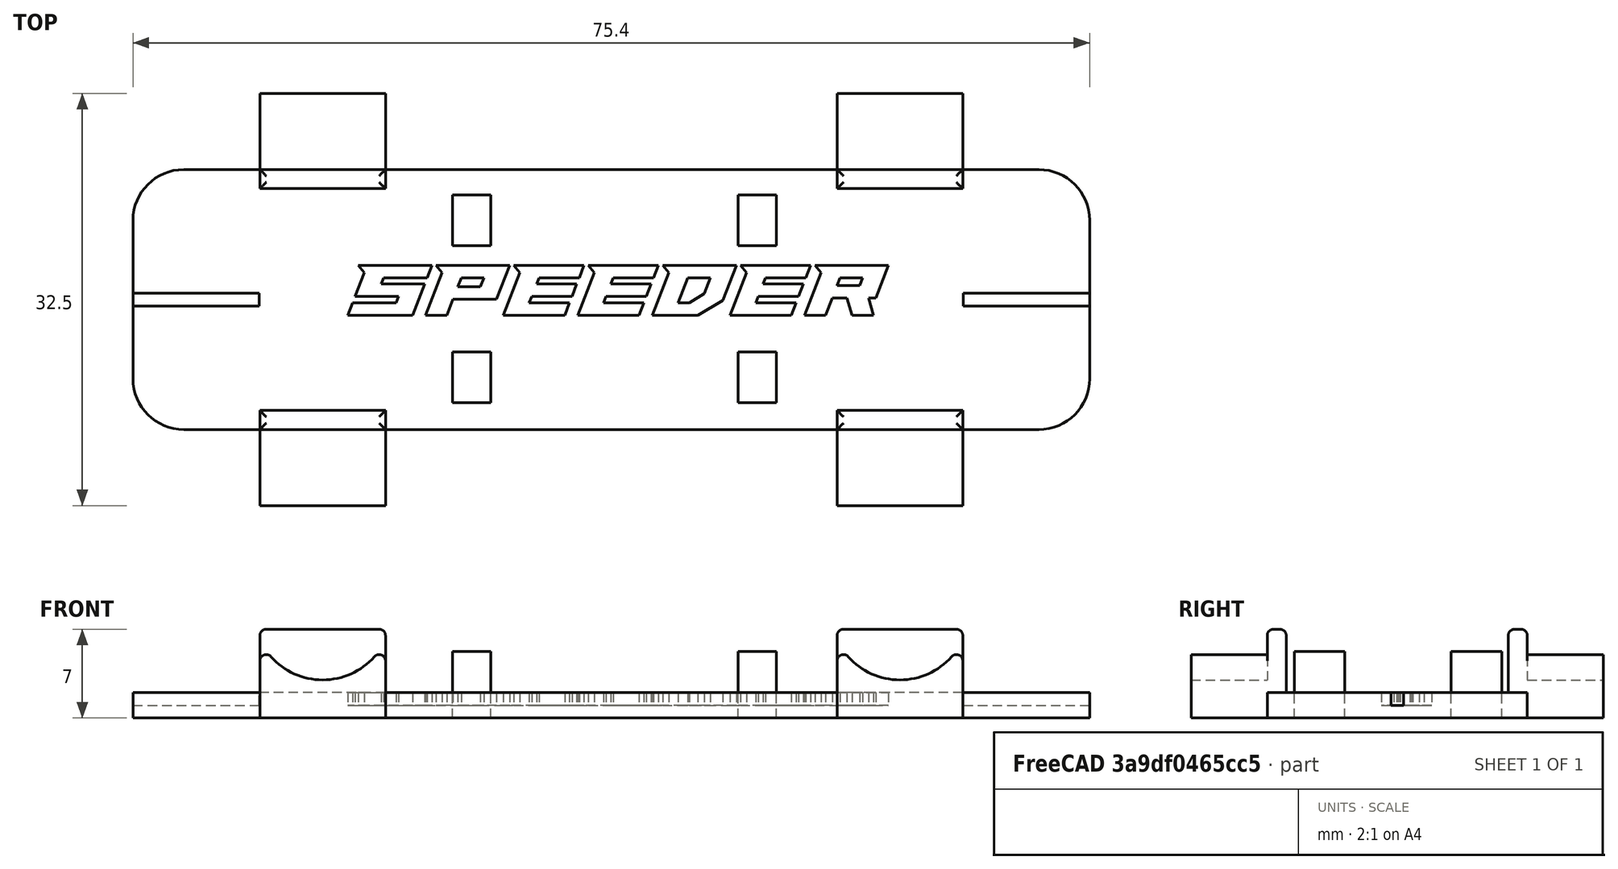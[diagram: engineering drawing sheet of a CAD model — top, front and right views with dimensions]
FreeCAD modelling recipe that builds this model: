
FCSTD DOCUMENT  (FreeCAD 0.19R24276 (Git))
Label: axleJig5
License: All rights reserved
LicenseURL: http://en.wikipedia.org/wiki/All_rights_reserved
objects: Part::Box×15, Part::Fillet×7, Part::Cut×6, Part::MultiFuse×4, Part::Cylinder×2, Spreadsheet::Sheet×1, Part::Part2DObjectPython×1, Part::Extrusion×1
note: 36 computed .brp shape members not serialized (recipe doc carries the construction recipe); baked Part::Feature solids carry a one-line shape summary decoded from their .brp

FEATURE [Part::Box] Box  label="Cube"
  AttacherType = Attacher::AttachEngine3D
  Height = 8
  Length = 9.9
  Placement = pos=(-4.95,0,0) rot=(0,0,1;0rad)
  Width = 32.5
  expr: Width = <<data>>.wheel_width * 2 + <<data>>.axle_width
  expr: Length = Spreadsheet.wheel_diameter_F - 1mm
  expr: .Placement.Base.x = -<<data>>.wheel_diameter_F / 2 + 0.5mm
FEATURE [Spreadsheet::Sheet] Spreadsheet  label="data"
  cells = A4=wheel_base; B4(wheel_base)==45.5mm; C4=add 0.5mm; D4==43.4mm; E4==46.2mm; F4==44.25mm; A5=axle_width; B5(axle_width)==20.5mm; C5=inside wheel-to-wheel; D5=21; E5=21.mm; F5==21mm; A6=wheel_well; B6(wheel_well)==17.5mm; D6==16.75mm; E6==17mm; F6=16.5; A7=ride_height_r; B7(ride_height_r)==2.25mm; D7==3.75mm; F7==2mm; A8=ride_height_f; B8(ride_height_f)==2.25mm; A9=axle_diameter; A10=post_wdith; A11=post_thickness; A12=wheel_diameter_F; B12(wheel_diameter_F)==10.9mm; D12==10.9mm; E12==10.9mm; F12==10.9mm; A13=wheel_diameter_R; B13(wheel_diameter_R)==10.9mm; D13==10.9mm; E13==10.9mm; F13==12.6mm; A14=wheel_width; B14(wheel_width)==6mm; D14==6mm; E14==6mm; F14=6; B15=Project; D15=Honda Civic Si; E15=Kia Stinger; F15=Rodger Dodger
FEATURE [Part::Cylinder] Cylinder
  Angle = 360
  AttacherType = Attacher::AttachEngine3D
  Height = 32.5
  Placement = pos=(0,0,8.45) rot=(-1,0,0;1.5708rad)
  Radius = 5.45
  expr: Radius = <<data>>.wheel_diameter_F / 2
  expr: Height = <<data>>.wheel_width * 2 + <<data>>.axle_width
  expr: .Placement.Base.z = <<data>>.wheel_diameter_F / 2 + 3mm
FEATURE [Part::Box] Box019  label="Cube017"
  AttacherType = Attacher::AttachEngine3D
  Height = 10
  Length = 9.9
  Placement = pos=(-4.95,6.5,2) rot=(0,0,1;0rad)
  Width = 18.5
  expr: .Placement.Base.y = <<data>>.wheel_width + (<<data>>.axle_width - <<data>>.wheel_well) / 2 - 1mm
  expr: Width = <<data>>.wheel_well + 1mm
  expr: Length = Spreadsheet.wheel_diameter_F - 1mm
  expr: .Placement.Base.x = -<<data>>.wheel_diameter_F / 2 + 0.5mm
FEATURE [Part::Cut] Cut
  Base = -> Box
  Tool = -> Cylinder
FEATURE [Part::Fillet] Fillet
  Base = -> Cut
  Edges = 2 edges r=0.5: [Edge2,Edge9]
FEATURE [Part::Box] Box020  label="FR spacer"
  AttacherType = Attacher::AttachEngine3D
  Height = 7
  Length = 9.9
  Placement = pos=(-4.95,6,0) rot=(0,0,1;0rad)
  Width = 1.5
  expr: Length = Spreadsheet.wheel_diameter_F - 1mm
  expr: .Placement.Base.x = -<<data>>.wheel_diameter_F / 2 + 0.5mm
  expr: .Placement.Base.y = <<data>>.wheel_width
  expr: Width = (<<data>>.axle_width - <<data>>.wheel_well) / 2
FEATURE [Part::Fillet] Fillet001
  Base = -> Box020
  Edges = 4 edges r=0.5: [Edge2,Edge6,Edge10,Edge12]
FEATURE [Part::Cut] Cut007
  Base = -> Fillet
  Tool = -> Box019
FEATURE [Part::Box] Box021  label="RL spacer"
  AttacherType = Attacher::AttachEngine3D
  Height = 7
  Length = 9.9
  Placement = pos=(-4.95,6,0) rot=(0,0,1;0rad)
  Width = 1.5
  expr: Width = (<<data>>.axle_width - <<data>>.wheel_well) / 2
  expr: .Placement.Base.y = <<data>>.wheel_width
  expr: .Placement.Base.x = -<<data>>.wheel_diameter_F / 2 + 0.5mm
  expr: Length = Spreadsheet.wheel_diameter_F - 1mm
FEATURE [Part::Fillet] Fillet002
  Base = -> Box021
  Edges = 4 edges r=0.5: [Edge2,Edge6,Edge10,Edge12]
  Placement = pos=(0,19,0) rot=(0,0,1;0rad)
  expr: .Placement.Base.y = <<data>>.axle_width - (<<data>>.axle_width - <<data>>.wheel_well) / 2
FEATURE [Part::MultiFuse] Fusion  label="FrontAxle"
  Placement = pos=(45.5,0,0) rot=(0,0,1;0rad)
  Shapes = -> [Fillet002,Cut007,Fillet001]
  expr: .Placement.Base.x = <<data>>.wheel_base
FEATURE [Part::Part2DObjectPython] ShapeString  # Draft 2D object (typed FeaturePython)
  FontFile = <userpath>/git/KiCad/Inkscape/fonts/Paladins-nl8P.otf
  Placement = pos=(1.26,15,2) rot=(0,0,1;0rad)
  Size = 2
  String = Speeder
  Tracking = 0
FEATURE [Part::Box] Box022  label="Cube020"
  AttacherType = Attacher::AttachEngine3D
  Height = 10
  Length = 9.9
  Placement = pos=(-4.95,6.5,2) rot=(0,0,1;0rad)
  Width = 18.5
  expr: .Placement.Base.x = -<<data>>.wheel_diameter_R / 2 + 0.5mm
  expr: Length = Spreadsheet.wheel_diameter_R - 1mm
  expr: Width = <<data>>.wheel_well + 1mm
  expr: .Placement.Base.y = <<data>>.wheel_width + (<<data>>.axle_width - <<data>>.wheel_well) / 2 - 1mm
FEATURE [Part::Box] Box023  label="Cube021"
  AttacherType = Attacher::AttachEngine3D
  Height = 7
  Length = 9.9
  Placement = pos=(-4.95,6,0) rot=(0,0,1;0rad)
  Width = 1.5
  expr: Width = (<<data>>.axle_width - <<data>>.wheel_well) / 2
  expr: .Placement.Base.y = <<data>>.wheel_width
  expr: .Placement.Base.x = -Spreadsheet.wheel_diameter_R / 2 + 0.5mm
  expr: Length = Spreadsheet.wheel_diameter_R - 1mm
FEATURE [Part::Fillet] Fillet004
  Base = -> Box023
  Edges = 4 edges r=0.5: [Edge2,Edge6,Edge10,Edge12]
FEATURE [Part::Box] Box024  label="Cube022"
  AttacherType = Attacher::AttachEngine3D
  Height = 7
  Length = 9.9
  Placement = pos=(-4.95,6,0) rot=(0,0,1;0rad)
  Width = 1.5
  expr: Length = Spreadsheet.wheel_diameter_R - 1mm
  expr: .Placement.Base.x = -<<data>>.wheel_diameter_R / 2 + 0.5mm
  expr: .Placement.Base.y = <<data>>.wheel_width
  expr: Width = (<<data>>.axle_width - <<data>>.wheel_well) / 2
FEATURE [Part::Fillet] Fillet005
  Base = -> Box024
  Edges = 4 edges r=0.5: [Edge2,Edge6,Edge10,Edge12]
  Placement = pos=(0,19,0) rot=(0,0,1;0rad)
  expr: .Placement.Base.y = <<data>>.axle_width - (<<data>>.axle_width - <<data>>.wheel_well) / 2
FEATURE [Part::Box] Box025  label="Cube023"
  AttacherType = Attacher::AttachEngine3D
  Height = 8
  Length = 9.9
  Placement = pos=(-4.95,0,0) rot=(0,0,1;0rad)
  Width = 32.5
  expr: .Placement.Base.x = -Spreadsheet.wheel_diameter_R / 2 + 0.5mm
  expr: Length = Spreadsheet.wheel_diameter_R - 1mm
  expr: Width = <<data>>.wheel_width * 2 + <<data>>.axle_width
FEATURE [Part::Cylinder] Cylinder002
  Angle = 360
  AttacherType = Attacher::AttachEngine3D
  Height = 32.5
  Placement = pos=(0,0,8.45) rot=(-1,0,0;1.5708rad)
  Radius = 5.45
  expr: .Placement.Base.z = <<data>>.wheel_diameter_R / 2 + 3mm
  expr: Height = <<data>>.wheel_width * 2 + <<data>>.axle_width
  expr: Radius = <<data>>.wheel_diameter_R / 2
FEATURE [Part::Cut] Cut008
  Base = -> Box025
  Tool = -> Cylinder002
FEATURE [Part::Fillet] Fillet003
  Base = -> Cut008
  Edges = 2 edges r=0.5: [Edge2,Edge9]
FEATURE [Part::Cut] Cut009
  Base = -> Fillet003
  Tool = -> Box022
FEATURE [Part::MultiFuse] Fusion001  label="RearAxle001"
  Shapes = -> [Fillet005,Cut009,Fillet004]
FEATURE [Part::Extrusion] Extrude
  Base = -> ShapeString
  Dir = (0,0,1)
  DirMode = 2
  FaceMakerClass = Part::FaceMakerBullseye
  LengthFwd = 1
  LengthRev = 0
  Reversed = true
  Solid = false
  Symmetric = false
FEATURE [Part::Box] Box026  label="Cube024"
  AttacherType = Attacher::AttachEngine3D
  Height = 1
  Length = 10
  Placement = pos=(-15,15.75,1) rot=(0,0,1;0rad)
  Width = 1
  expr: .Placement.Base.y = (<<data>>.wheel_width * 2 + <<data>>.axle_width) / 2 - 0.5mm
FEATURE [Part::Box] Box027  label="Cube025"
  AttacherType = Attacher::AttachEngine3D
  Height = 1
  Length = 10
  Placement = pos=(50.5,15.75,1) rot=(0,0,1;0rad)
  Width = 1
  expr: .Placement.Base.y = (<<data>>.wheel_width * 2 + <<data>>.axle_width) / 2 - 0.5mm
  expr: .Placement.Base.x = <<data>>.wheel_base + 5mm
FEATURE [Part::Box] Box008  label="base"
  AttacherType = Attacher::AttachEngine3D
  Height = 2
  Length = 75.4
  Placement = pos=(-14.95,6,0) rot=(0,0,1;0rad)
  Width = 20.5
  expr: .Placement.Base.y = <<data>>.wheel_width
  expr: Height = 2mm
  expr: Width = <<data>>.axle_width
  expr: Length = <<data>>.wheel_diameter_F / 2 + <<data>>.wheel_base + <<data>>.wheel_diameter_R / 2 - 1mm + 20mm
  expr: .Placement.Base.x = -<<data>>.wheel_diameter_F / 2 + 0.5mm - 10mm
FEATURE [Part::Fillet] Fillet006
  Base = -> Box008
  Edges = 4 edges r=4: [Edge1,Edge3,Edge5,Edge7]
FEATURE [Part::MultiFuse] Fusion002
  Shapes = -> [Box027,Box026]
FEATURE [Part::Cut] Cut010
  Base = -> Fillet006
  Tool = -> Fusion002
FEATURE [Part::Box] Box028  label="Cube026"
  AttacherType = Attacher::AttachEngine3D
  Height = 5.25
  Length = 3
  Placement = pos=(10.25,8.125,0) rot=(0,0,1;0rad)
  Width = 4
  expr: .Placement.Base.y = (<<data>>.wheel_width + <<data>>.axle_width / 2) / 2
  expr: .Placement.Base.x = <<data>>.wheel_base / 2 - 12.5mm
  expr: Height = Spreadsheet.ride_height_r + 3mm
FEATURE [Part::Box] Box029  label="Cube027"
  AttacherType = Attacher::AttachEngine3D
  Height = 5.25
  Length = 3
  Placement = pos=(10.25,20.5,0) rot=(0,0,1;0rad)
  Width = 4
  expr: Height = Spreadsheet.ride_height_r + 3mm
  expr: .Placement.Base.x = <<data>>.wheel_base / 2 - 12.5mm
  expr: .Placement.Base.y = <<data>>.wheel_width + <<data>>.axle_width / 2 + <<data>>.axle_width / 2 - 6mm
FEATURE [Part::Box] Box030  label="Cube028"
  AttacherType = Attacher::AttachEngine3D
  Height = 5.25
  Length = 3
  Placement = pos=(32.75,8.125,0) rot=(0,0,1;0rad)
  Width = 4
  expr: Height = Spreadsheet.ride_height_f + 3mm
  expr: .Placement.Base.x = <<data>>.wheel_base / 2 + 10mm
  expr: .Placement.Base.y = (<<data>>.wheel_width + <<data>>.axle_width / 2) / 2
FEATURE [Part::Box] Box031  label="Cube029"
  AttacherType = Attacher::AttachEngine3D
  Height = 5.25
  Length = 3
  Placement = pos=(32.75,20.5,0) rot=(0,0,1;0rad)
  Width = 4
  expr: .Placement.Base.y = <<data>>.wheel_width + <<data>>.axle_width / 2 + <<data>>.axle_width / 2 - 6mm
  expr: .Placement.Base.x = <<data>>.wheel_base / 2 + 10mm
  expr: Height = Spreadsheet.ride_height_f + 3mm
FEATURE [Part::MultiFuse] Fusion003
  Shapes = -> [Cut010,Fusion001,Fusion]
FEATURE [Part::Cut] Cut011
  Base = -> Fusion003
  Tool = -> Extrude
